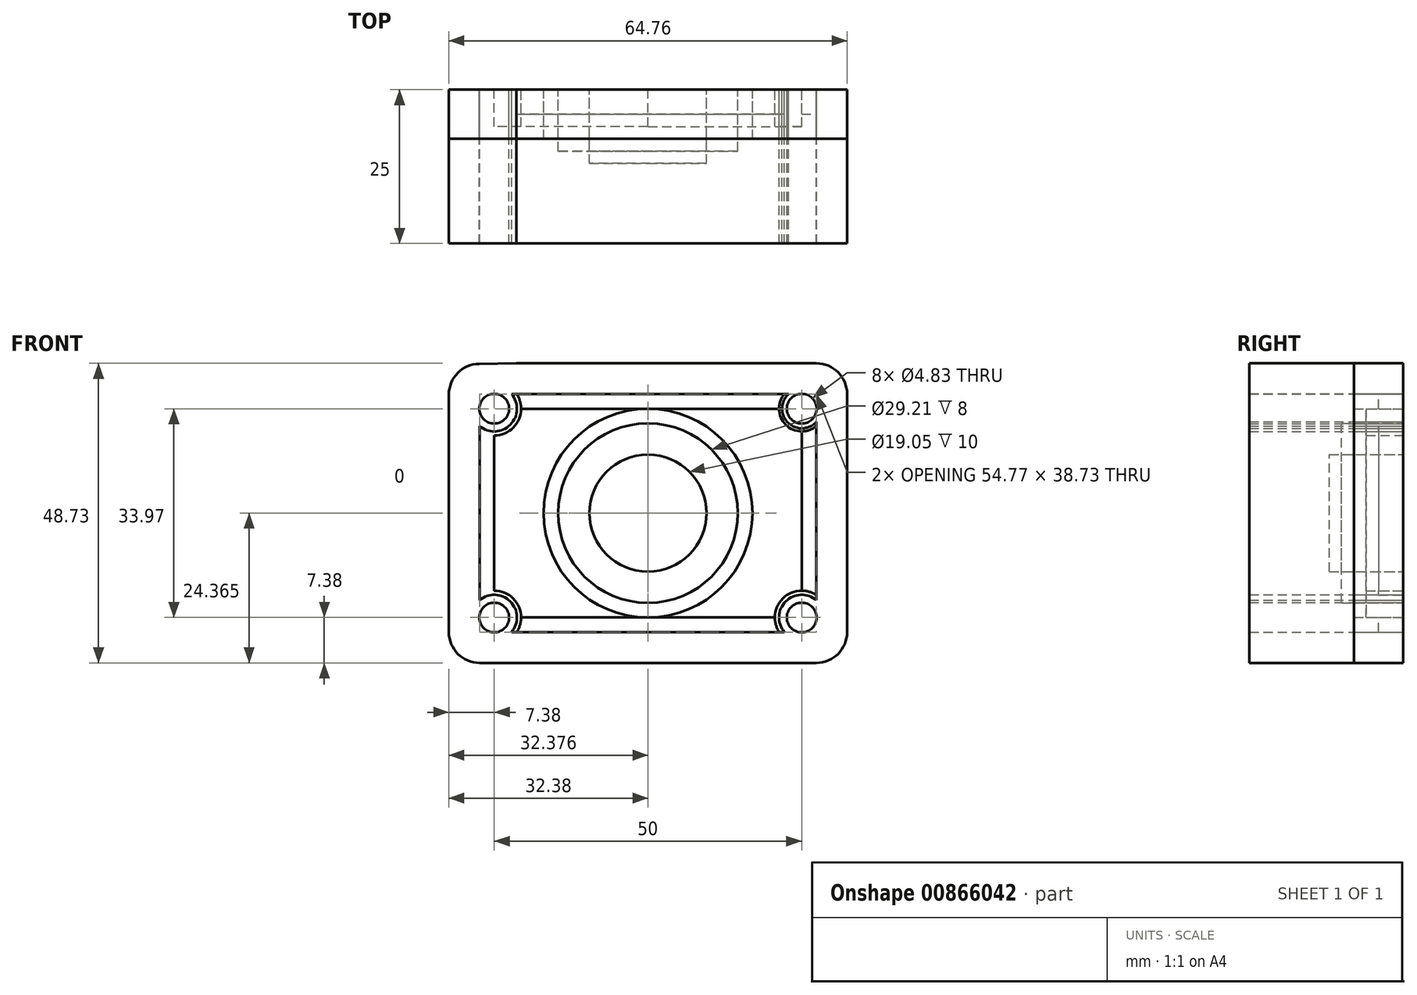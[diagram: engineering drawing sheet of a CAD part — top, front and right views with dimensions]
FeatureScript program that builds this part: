
annotation { "Feature Type Name" : "Feature", "Feature Type Description" : "" }
export const myFeature = defineFeature(function(context is Context, id is Id, definition is map)
    precondition{}
    {
        {
            var Q0;
            Q0=qCreatedBy(makeId("Front.planeOp"),FACE);
            var sketch = newSketch(context, id + "F0", { "sketchPlane" : qUnion([Q0])});
            skCircle(sketch, "E0", {"center": v(25, 0.52) * mm, "radius": 9.53 * mm});
            skCircle(sketch, "E1", {"center": v(25, 0.52) * mm, "radius": 14.6 * mm});
            skCircle(sketch, "E2", {"center": v(25, 0.52) * mm, "radius": 16.98 * mm});
            skLineSegment(sketch, "E3", {"start": v(25, 17.5) * mm, "end": v(46.8, 17.5) * mm});
            skLineSegment(sketch, "E4", {"start": v(25, 17.5) * mm, "end": v(4.37, 17.5) * mm});
            skLineSegment(sketch, "E5", {"start": v(25, -16.46) * mm, "end": v(46.31, -16.46) * mm});
            skLineSegment(sketch, "E6", {"start": v(25, -16.46) * mm, "end": v(3.69, -16.46) * mm});
            skLineSegment(sketch, "E7", {"start": v(50, 14.31) * mm, "end": v(50, -12.77) * mm});
            skLineSegment(sketch, "E8", {"start": v(0, -12.77) * mm, "end": v(0, 13.14) * mm});
            skLineSegment(sketch, "E9", {"start": v(-2.38, 17.5) * mm, "end": v(-2.38, 17.1) * mm});
            skLineSegment(sketch, "E10", {"start": v(-2.38, 17.5) * mm, "end": v(-2.38, 17.92) * mm});
            skLineSegment(sketch, "E11", {"start": v(-0.4, 19.89) * mm, "end": v(0.4, 19.89) * mm});
            skLineSegment(sketch, "E12", {"start": v(52.38, -16.46) * mm, "end": v(52.38, -16.87) * mm});
            skLineSegment(sketch, "E13", {"start": v(-2.38, -16.46) * mm, "end": v(-2.38, -16.87) * mm});
            skLineSegment(sketch, "E14", {"start": v(-0.4, -18.84) * mm, "end": v(0.4, -18.84) * mm});
            skCircle(sketch, "E15", {"center": v(0, -16.46) * mm, "radius": 2.42 * mm});
            skCircle(sketch, "E16", {"center": v(0, 17.5) * mm, "radius": 2.42 * mm});
            skCircle(sketch, "E17", {"center": v(50, 17.5) * mm, "radius": 2.42 * mm});
            skCircle(sketch, "E18", {"center": v(50, -16.46) * mm, "radius": 2.42 * mm});
            skArc(sketch, "E19", {"start": v(-2.38, 13.85) * mm, "mid": v(3.09, 14.42) * mm, "end": v(3.66, 19.89) * mm});
            skPoint(sketch, "E20.orphan", {"position": v(-2.38, 19.89) * mm});
            skLineSegment(sketch, "E21.trimOffspring", {"start": v(-2.38, 13.85) * mm, "end": v(-2.38, -13.64) * mm});
            skLineSegment(sketch, "E22", {"start": v(0, 0) * mm, "end": v(0, 10.6) * mm});
            skLineSegment(sketch, "E23", {"start": v(0, 0) * mm, "end": v(0, -10.6) * mm});
            skLineSegment(sketch, "E24.trimOffspring", {"start": v(4.37, 17.5) * mm, "end": v(6.92, 17.5) * mm});
            skLineSegment(sketch, "E25.trimOffspring", {"start": v(3.66, 19.89) * mm, "end": v(47.87, 19.89) * mm});
            skArc(sketch, "E26", {"start": v(-2.39, 14.7) * mm, "mid": v(2.6, 14.9) * mm, "end": v(2.82, 19.89) * mm});
            skLineSegment(sketch, "E27", {"start": v(2.82, 19.89) * mm, "end": v(4.36, 19.89) * mm});
            skLineSegment(sketch, "E28", {"start": v(-2.38, 13.85) * mm, "end": v(-2.39, 14.7) * mm});
            skArc(sketch, "E29", {"start": v(47.87, 19.89) * mm, "mid": v(47.74, 15.25) * mm, "end": v(52.38, 15.38) * mm});
            skArc(sketch, "E30", {"start": v(47.18, 19.89) * mm, "mid": v(47.4, 14.9) * mm, "end": v(52.38, 14.69) * mm});
            skLineSegment(sketch, "E31.trimOffspring", {"start": v(52.38, 15.38) * mm, "end": v(52.38, -13.64) * mm});
            skLineSegment(sketch, "E32", {"start": v(50, 19.92) * mm, "end": v(49.92, 19.92) * mm});
            skLineSegment(sketch, "E33", {"start": v(-7.38, 0) * mm, "end": v(-7.38, 19.81) * mm});
            skLineSegment(sketch, "E34", {"start": v(57.38, 0) * mm, "end": v(57.38, 19.89) * mm});
            skLineSegment(sketch, "E35", {"start": v(3.6, 24.89) * mm, "end": v(52.38, 24.89) * mm});
            skLineSegment(sketch, "E36", {"start": v(3.6, 24.89) * mm, "end": v(-2.45, 24.8) * mm});
            skLineSegment(sketch, "E37", {"start": v(-7.38, 23.87) * mm, "end": v(-7.4, 24.74) * mm});
            skLineSegment(sketch, "E38", {"start": v(52.38, -23.84) * mm, "end": v(52.38, -23.84) * mm});
            skLineSegment(sketch, "E39", {"start": v(57.38, -18.84) * mm, "end": v(57.38, 0) * mm});
            skLineSegment(sketch, "E40", {"start": v(-2.38, -23.84) * mm, "end": v(-2.38, -23.84) * mm});
            skLineSegment(sketch, "E41", {"start": v(-7.38, -18.84) * mm, "end": v(-7.38, -18.84) * mm});
            skLineSegment(sketch, "E42", {"start": v(-2.38, -23.84) * mm, "end": v(52.38, -23.84) * mm});
            skLineSegment(sketch, "E43", {"start": v(-7.38, -18.84) * mm, "end": v(-7.38, 0) * mm});
            skArc(sketch, "E44", {"start": v(2.82, -18.84) * mm, "mid": v(2.6, -13.85) * mm, "end": v(-2.38, -13.64) * mm});
            skArc(sketch, "E45", {"start": v(3.66, -18.84) * mm, "mid": v(3.09, -13.37) * mm, "end": v(-2.38, -12.8) * mm});
            skArc(sketch, "E46", {"start": v(52.38, -13.64) * mm, "mid": v(47.4, -13.85) * mm, "end": v(47.18, -18.84) * mm});
            skArc(sketch, "E47", {"start": v(52.38, -12.8) * mm, "mid": v(46.91, -13.37) * mm, "end": v(46.34, -18.84) * mm});
            skLineSegment(sketch, "E48.trimOffspring", {"start": v(52.38, -16.05) * mm, "end": v(52.38, -16.46) * mm});
            skLineSegment(sketch, "E49.trimOffspring", {"start": v(49.6, -18.84) * mm, "end": v(50.4, -18.84) * mm});
            skLineSegment(sketch, "E50.trimOffspring", {"start": v(2.82, -18.84) * mm, "end": v(47.18, -18.84) * mm});
            skLineSegment(sketch, "E51.trimOffspring", {"start": v(-2.38, -16.05) * mm, "end": v(-2.38, -16.46) * mm});
            skPoint(sketch, "E52.start.orphan", {"position": v(-2.38, 0) * mm});
            skPoint(sketch, "E53.start.orphan", {"position": v(52.38, 0) * mm});
            skArc(sketch, "E54.filletArc", {"start": v(-2.45, 24.8) * mm, "mid": v(-5.94, 23.32) * mm, "end": v(-7.38, 19.81) * mm});
            skPoint(sketch, "E55.visualSharp", {"position": v(57.38, 24.89) * mm});
            skArc(sketch, "E55.filletArc", {"start": v(57.38, 19.89) * mm, "mid": v(55.92, 23.42) * mm, "end": v(52.38, 24.89) * mm});
            skPoint(sketch, "E56.visualSharp", {"position": v(57.38, -23.84) * mm});
            skArc(sketch, "E56.filletArc", {"start": v(52.38, -23.84) * mm, "mid": v(55.92, -22.38) * mm, "end": v(57.38, -18.84) * mm});
            skPoint(sketch, "E57.visualSharp", {"position": v(-7.38, -23.84) * mm});
            skArc(sketch, "E57.filletArc", {"start": v(-7.38, -18.84) * mm, "mid": v(-5.92, -22.38) * mm, "end": v(-2.38, -23.84) * mm});
            skSolve(sketch);
        }
        {
            var Q0;
            Q0=makeQuery(id+"F0.imprint","IMPRINT",FACE,{"disambiguationData":[TD([[makeQuery(id+"F0.imprint","IMPRINT",EDGE,{"derivedFrom":sQuery(id+"F0.wireOp",EDGE,"E0")}),1.0]])]});
            extrude(context, id + "F1", {"entities" : qUnion([Q0]), "depth" : 12 * mm, "offsetDistance" : 25 * mm});
        }
        {
            var Q0;
            Q0=qSketchRegion(id+"F0",true);
            extrude(context, id + "F2", {"entities" : qUnion([Q0]), "operationType" : NewBodyOperationType.ADD, "depth" : 25 * mm, "offsetDistance" : 25 * mm});
        }
        {
            var Q0;
            {var subQ9=sQuery(id+"F0.wireOp",EDGE,"E4");Q0=makeQuery(id+"F0.imprint","IMPRINT",FACE,{"disambiguationData":[TD([[makeQuery(id+"F0.imprint","IMPRINT",EDGE,{"derivedFrom":subQ9}),1.0]])]});}
            var Q1;
            {var subQ0=sQuery(id+"F0.wireOp",EDGE,"E30");var subQ1=sQuery(id+"F0.wireOp",EDGE,"E7");var subQ2=makeQuery(id+"F0.imprint","INTERSECT",VERTEX,{"derivedFrom":[subQ1,subQ0]});Q1=makeQuery(id+"F0.imprint","IMPRINT",FACE,{"disambiguationData":[TD([[makeQuery(id+"F0.imprint","IMPRINT",EDGE,{"disambiguationData":[TD([[subQ2,-1.0]])],"derivedFrom":subQ1}),-1.0]])]});}
            extrude(context, id + "F3", {"entities" : qUnion([Q0, Q1]), "depth" : 6 * mm, "offsetDistance" : 25 * mm});
        }
        {
            var Q0;
            Q0=makeQuery(id+"F0.imprint","IMPRINT",FACE,{"disambiguationData":[TD([[makeQuery(id+"F0.imprint","IMPRINT",EDGE,{"derivedFrom":sQuery(id+"F0.wireOp",EDGE,"E1")}),-1.0]])]});
            extrude(context, id + "F4", {"entities" : qUnion([Q0]), "depth" : 8 * mm, "offsetDistance" : 25 * mm});
        }
        {
            var Q0;
            Q0=makeQuery(id+"F0.imprint","IMPRINT",FACE,{"disambiguationData":[TD([[makeQuery(id+"F0.imprint","IMPRINT",EDGE,{"derivedFrom":sQuery(id+"F0.wireOp",EDGE,"E0")}),-1.0]])]});
            extrude(context, id + "F5", {"entities" : qUnion([Q0]), "depth" : 10 * mm, "offsetDistance" : 25 * mm});
        }
        {
            var Q0;
            {var subQ40=sQuery(id+"F0.wireOp",EDGE,"E26");Q0=makeQuery(id+"F0.imprint","IMPRINT",FACE,{"disambiguationData":[TD([[makeQuery(id+"F0.imprint","IMPRINT",EDGE,{"derivedFrom":subQ40}),1.0]])]});}
            extrude(context, id + "F6", {"entities" : qUnion([Q0]), "depth" : 8 * mm, "offsetDistance" : 25 * mm});
        }
        {
            var Q0;
            {var subQ0=sQuery(id+"F0.wireOp",EDGE,"E50.trimOffspring");var subQ5=sQuery(id+"F0.wireOp",EDGE,"E45");var subQ6=makeQuery(id+"F0.imprint","INTERSECT",VERTEX,{"derivedFrom":[subQ5,subQ0]});Q0=makeQuery(id+"F0.imprint","IMPRINT",FACE,{"disambiguationData":[TD([[makeQuery(id+"F0.imprint","IMPRINT",EDGE,{"disambiguationData":[TD([[subQ6,-1.0]])],"derivedFrom":subQ5}),-1.0]])]});}
            var Q1;
            {var subQ8=sQuery(id+"F0.wireOp",EDGE,"E22");Q1=makeQuery(id+"F0.imprint","IMPRINT",FACE,{"disambiguationData":[TD([[makeQuery(id+"F0.imprint","IMPRINT",EDGE,{"derivedFrom":subQ8}),1.0]])]});}
            var Q2;
            {var subQ0=sQuery(id+"F0.wireOp",EDGE,"E4");Q2=makeQuery(id+"F0.imprint","IMPRINT",FACE,{"disambiguationData":[TD([[makeQuery(id+"F0.imprint","IMPRINT",EDGE,{"derivedFrom":subQ0}),-1.0]])]});}
            var Q3;
            {var subQ0=sQuery(id+"F0.wireOp",EDGE,"E30");var subQ1=sQuery(id+"F0.wireOp",EDGE,"E7");var subQ2=makeQuery(id+"F0.imprint","INTERSECT",VERTEX,{"derivedFrom":[subQ1,subQ0]});Q3=makeQuery(id+"F0.imprint","IMPRINT",FACE,{"disambiguationData":[TD([[makeQuery(id+"F0.imprint","IMPRINT",EDGE,{"disambiguationData":[TD([[subQ2,-1.0]])],"derivedFrom":subQ1}),1.0]])]});}
            extrude(context, id + "F7", {"entities" : qUnion([Q0, Q1, Q2, Q3]), "depth" : 4 * mm, "offsetDistance" : 25 * mm});
        }
    });
